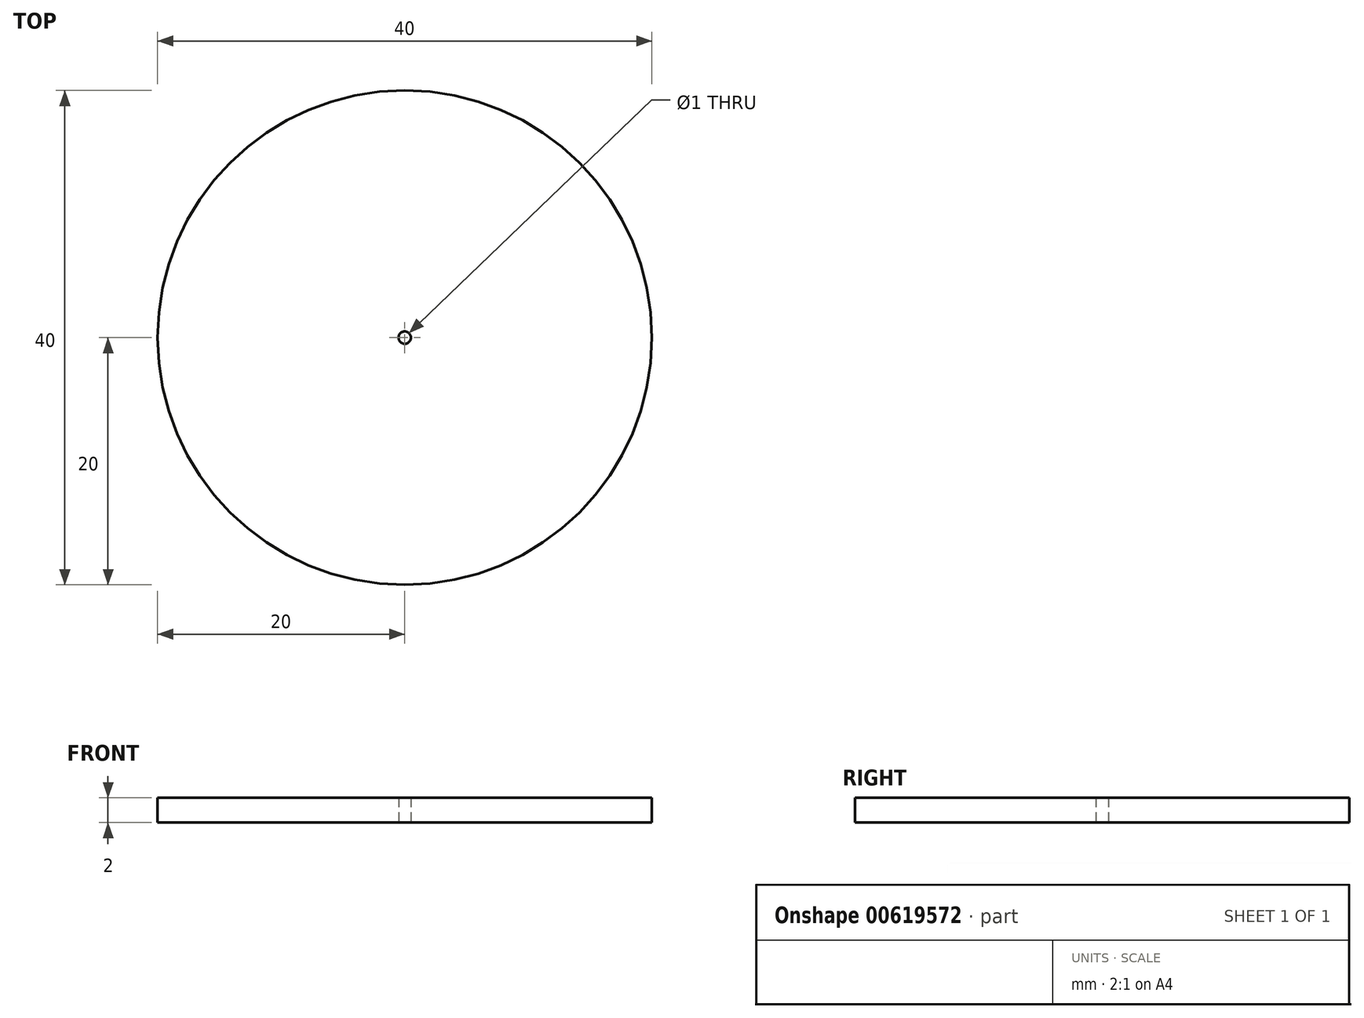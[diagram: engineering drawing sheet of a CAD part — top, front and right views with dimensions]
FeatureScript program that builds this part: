
annotation { "Feature Type Name" : "Feature", "Feature Type Description" : "" }
export const myFeature = defineFeature(function(context is Context, id is Id, definition is map)
    precondition{}
    {
        {
            var Q0;
            Q0=qCreatedBy(makeId("Top.planeOp"), FACE);
            var sketch = newSketch(context, id + "F0", { "sketchPlane" : qUnion([Q0])});
            skCircle(sketch, "E0", {"center": v(0, 0) * mm, "radius": 0.5 * mm});
            skCircle(sketch, "E1", {"center": v(0, 0) * mm, "radius": 20 * mm});
            skSolve(sketch);
        }
        {
            var Q0;
            Q0 = qSketchRegion(id + "F0", true);
            extrude(context, id + "F1", {"entities" : qUnion([Q0]), "depth" : 2 * mm, "offsetDistance" : 25 * mm});
        }
    });
